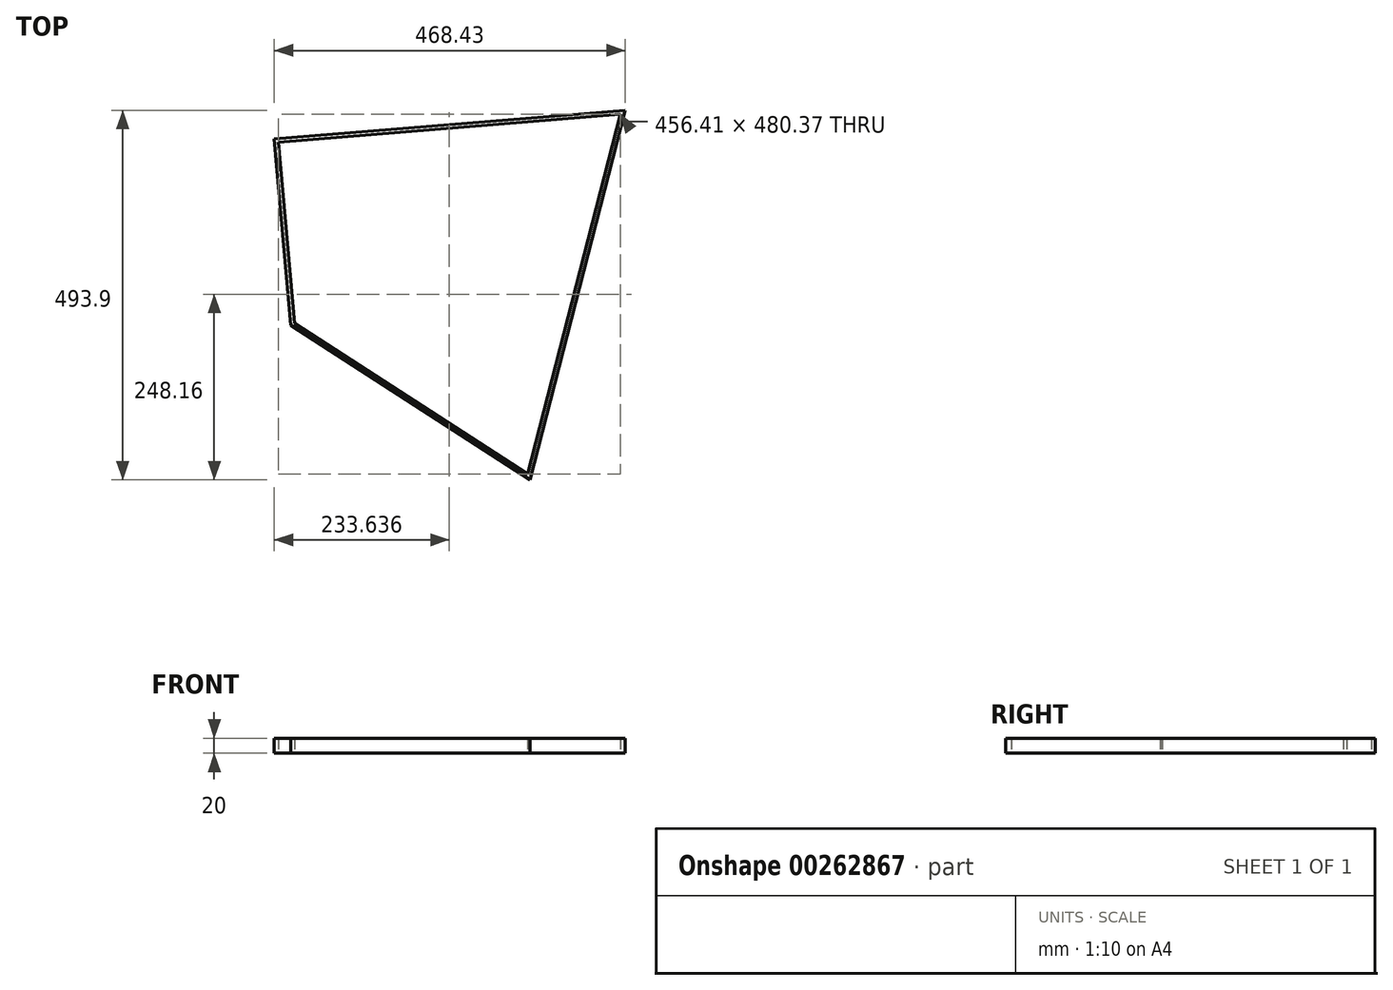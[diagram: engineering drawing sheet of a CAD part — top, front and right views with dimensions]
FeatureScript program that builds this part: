
annotation { "Feature Type Name" : "Feature", "Feature Type Description" : "" }
export const myFeature = defineFeature(function(context is Context, id is Id, definition is map)
    precondition{}
    {
        {
            var Q0;
            Q0=qCreatedBy(makeId("Top.planeOp"),FACE);
            var sketch = newSketch(context, id + "F0", { "sketchPlane" : qUnion([Q0])});
            skLineSegment(sketch, "E0", {"start": v(260.42, 204.91) * mm, "end": v(-208, 166.54) * mm});
            skLineSegment(sketch, "E1", {"start": v(260.42, 204.91) * mm, "end": v(133.28, -288.99) * mm});
            skLineSegment(sketch, "E2", {"start": v(133.28, -288.99) * mm, "end": v(-185.7, -82.46) * mm});
            skLineSegment(sketch, "E3", {"start": v(-185.7, -82.46) * mm, "end": v(-208, 166.54) * mm});
            skLineSegment(sketch, "E4.0", {"start": v(130.17, -281.02) * mm, "end": v(-180.94, -79.6) * mm});
            skLineSegment(sketch, "E4.1", {"start": v(253.83, 199.36) * mm, "end": v(130.17, -281.02) * mm});
            skLineSegment(sketch, "E4.2", {"start": v(253.83, 199.36) * mm, "end": v(-202.58, 161.97) * mm});
            skLineSegment(sketch, "E4.3", {"start": v(-180.94, -79.6) * mm, "end": v(-202.58, 161.97) * mm});
            skSolve(sketch);
        }
        {
            var Q0;
            Q0=makeQuery(id+"F0.imprint","IMPRINT",FACE,{"disambiguationData":[TD([[makeQuery(id+"F0.imprint","IMPRINT",EDGE,{"derivedFrom":sQuery(id+"F0.wireOp",EDGE,"E0")}),1.0]])]});
            extrude(context, id + "F1", {"entities" : qUnion([Q0]), "depth" : 20 * mm});
        }
    });
